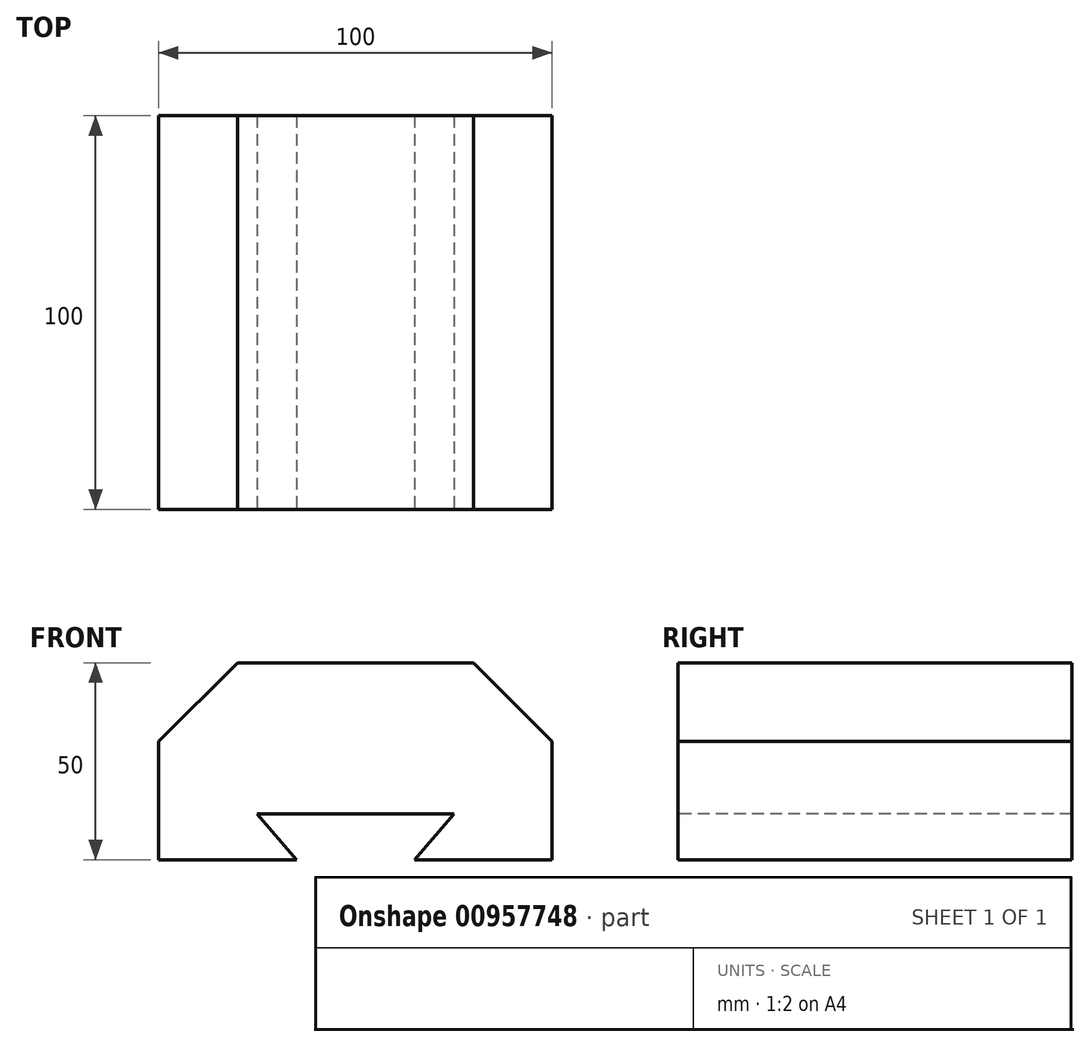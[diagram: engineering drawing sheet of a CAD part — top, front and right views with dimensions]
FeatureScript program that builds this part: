
annotation { "Feature Type Name" : "Feature", "Feature Type Description" : "" }
export const myFeature = defineFeature(function(context is Context, id is Id, definition is map)
    precondition{}
    {
        {
            var Q0;
            Q0=qCreatedBy(makeId("Front.planeOp"),FACE);
            var sketch = newSketch(context, id + "F0", { "sketchPlane" : qUnion([Q0])});
            skLineSegment(sketch, "E0", {"start": v(0, 60.84) * mm, "end": v(0, -21.33) * mm, "construction": true});
            skLineSegment(sketch, "E1", {"start": v(0, 11.69) * mm, "end": v(-25, 11.69) * mm});
            skLineSegment(sketch, "E2", {"start": v(-25, 11.69) * mm, "end": v(-15, 0) * mm});
            skLineSegment(sketch, "E3", {"start": v(-15, 0) * mm, "end": v(-50, 0) * mm});
            skLineSegment(sketch, "E4", {"start": v(-50, 0) * mm, "end": v(-50, 30) * mm});
            skLineSegment(sketch, "E5", {"start": v(-50, 30) * mm, "end": v(-30, 50) * mm});
            skLineSegment(sketch, "E6", {"start": v(-30, 50) * mm, "end": v(0, 50) * mm});
            skLineSegment(sketch, "E7.MirrorCS", {"start": v(25, 11.69) * mm, "end": v(15, 0) * mm});
            skLineSegment(sketch, "E8.MirrorCS", {"start": v(30, 50) * mm, "end": v(0, 50) * mm});
            skLineSegment(sketch, "E9.MirrorCS", {"start": v(15, 0) * mm, "end": v(50, 0) * mm});
            skLineSegment(sketch, "E10.MirrorCS", {"start": v(50, 30) * mm, "end": v(30, 50) * mm});
            skLineSegment(sketch, "E11.MirrorCS", {"start": v(0, 11.69) * mm, "end": v(25, 11.69) * mm});
            skLineSegment(sketch, "E12.MirrorCS", {"start": v(50, 0) * mm, "end": v(50, 30) * mm});
            skSolve(sketch);
        }
        {
            var Q0;
            Q0=makeQuery(id+"F0.imprint","IMPRINT",FACE,{"disambiguationData":[TD([[makeQuery(id+"F0.imprint","IMPRINT",EDGE,{"derivedFrom":sQuery(id+"F0.wireOp",EDGE,"E1")}),-1.0]])]});
            extrude(context, id + "F1", {"entities" : qUnion([Q0]), "oppositeDirection" : true, "depth" : 100 * mm, "offsetDistance" : 25 * mm});
        }
    });
